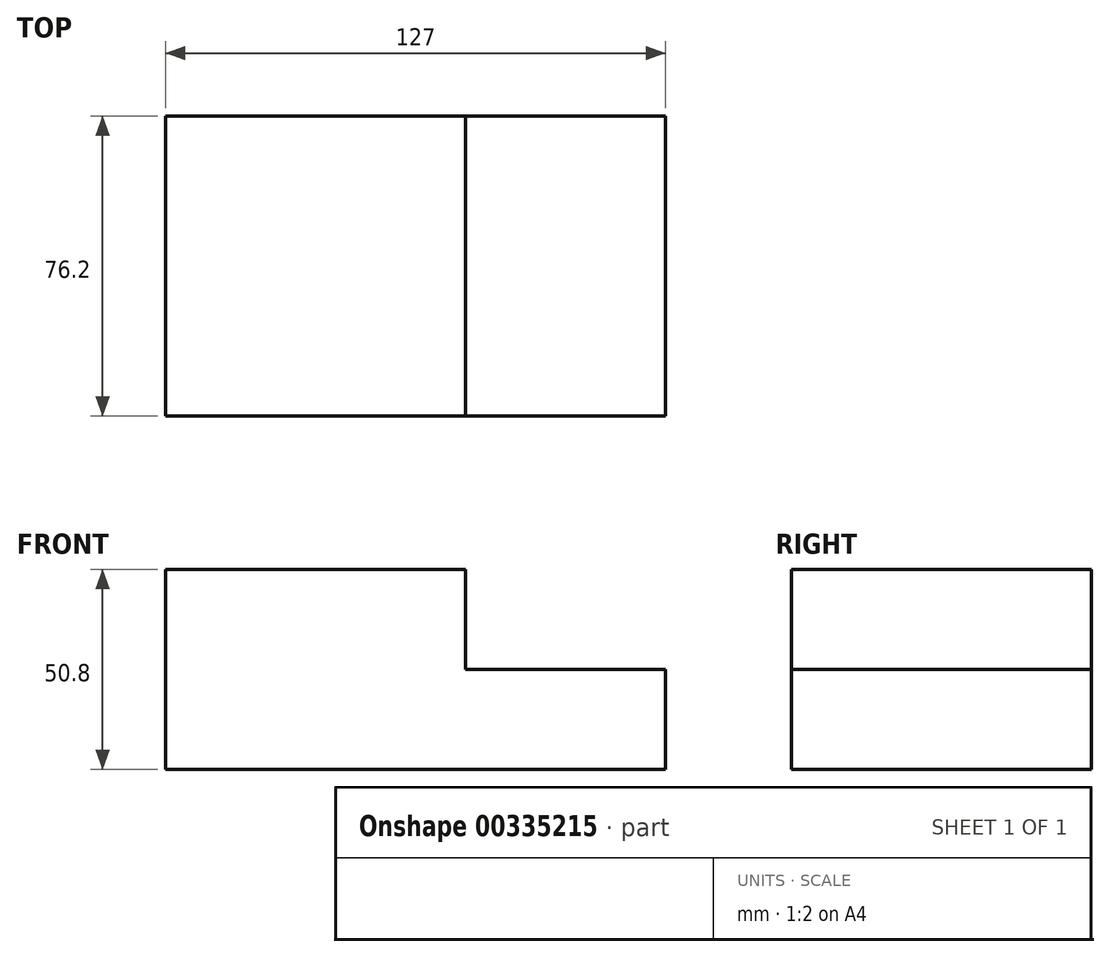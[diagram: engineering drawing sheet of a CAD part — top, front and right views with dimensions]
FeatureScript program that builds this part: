
annotation { "Feature Type Name" : "Feature", "Feature Type Description" : "" }
export const myFeature = defineFeature(function(context is Context, id is Id, definition is map)
    precondition{}
    {
        {
            var Q0;
            Q0=qCreatedBy(makeId("Front.planeOp"),FACE);
            var sketch = newSketch(context, id + "F0", { "sketchPlane" : qUnion([Q0])});
            skLineSegment(sketch, "E0", {"start": v(0, 0) * mm, "end": v(0, 50.8) * mm});
            skLineSegment(sketch, "E1", {"start": v(0, 50.8) * mm, "end": v(76.2, 50.8) * mm});
            skLineSegment(sketch, "E2", {"start": v(76.2, 50.8) * mm, "end": v(76.2, 25.4) * mm});
            skLineSegment(sketch, "E3", {"start": v(76.2, 25.4) * mm, "end": v(127, 25.4) * mm});
            skLineSegment(sketch, "E4", {"start": v(127, 25.4) * mm, "end": v(127, 0) * mm});
            skLineSegment(sketch, "E5", {"start": v(127, 0) * mm, "end": v(0, 0) * mm});
            skSolve(sketch);
        }
        {
            var Q0;
            Q0 = qSketchRegion(id + "F0", true);
            extrude(context, id + "F1", {"entities" : qUnion([Q0]), "depth" : 76.2 * mm});
        }
    });
